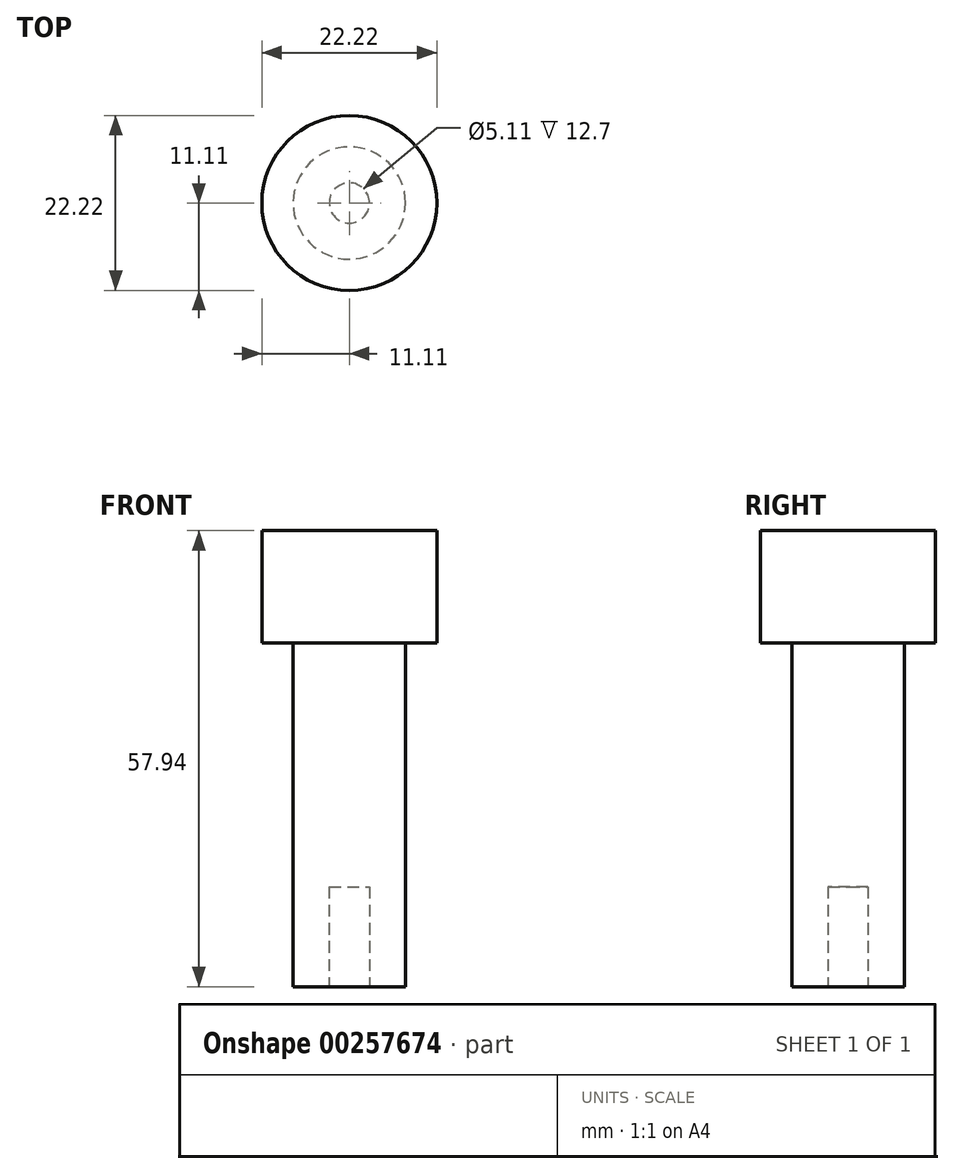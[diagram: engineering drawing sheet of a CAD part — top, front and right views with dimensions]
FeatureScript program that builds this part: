
annotation { "Feature Type Name" : "Feature", "Feature Type Description" : "" }
export const myFeature = defineFeature(function(context is Context, id is Id, definition is map)
    precondition{}
    {
        {
            var Q0;
            Q0=qCreatedBy(makeId("Top.planeOp"),FACE);
            var sketch = newSketch(context, id + "F0", { "sketchPlane" : qUnion([Q0])});
            skCircle(sketch, "E0", {"center": v(0, 0) * mm, "radius": 11.11 * mm});
            skSolve(sketch);
        }
        {
            var Q0;
            Q0=makeQuery(id+"F0.imprint","IMPRINT",FACE,{"disambiguationData":[TD([[makeQuery(id+"F0.imprint","IMPRINT",EDGE,{"derivedFrom":sQuery(id+"F0.wireOp",EDGE,"E0")}),1.0]])]});
            extrude(context, id + "F1", {"entities" : qUnion([Q0]), "endBound" : BoundingType.SYMMETRIC, "depth" : 14.27 * mm});
        }
        {
            var Q0;
            Q0=qCreatedBy(makeId("Top.planeOp"),FACE);
            var sketch = newSketch(context, id + "F2", { "sketchPlane" : qUnion([Q0])});
            skCircle(sketch, "E1", {"center": v(0, 0) * mm, "radius": 7.14 * mm});
            skSolve(sketch);
        }
        {
            var Q0;
            Q0 = qSketchRegion(id + "F2", true);
            var Q1;
            Q1=sQuery(id+"F2.wireOp",EDGE,"E1");
            extrude(context, id + "F3", {"entities" : qUnion([Q0]), "operationType" : NewBodyOperationType.ADD, "surfaceEntities" : qUnion([Q1]), "oppositeDirection" : true, "depth" : 50.8 * mm});
        }
        {
            var Q0;
            Q0=makeQuery(id+"F3.opExtrude","CAP_FACE",FACE,{"disambiguationData":[OSD([sQuery(id+"F2.wireOp",EDGE,"E1")])],"isStart":false});
            var sketch = newSketch(context, id + "F4", { "sketchPlane" : qUnion([Q0])});
            skCircle(sketch, "E2", {"center": v(0, 0) * mm, "radius": 2.55 * mm});
            skSolve(sketch);
        }
        {
            var Q0;
            Q0=makeQuery(id+"F4.imprint","IMPRINT",FACE,{"disambiguationData":[TD([[makeQuery(id+"F4.imprint","IMPRINT",EDGE,{"derivedFrom":sQuery(id+"F4.wireOp",EDGE,"E2")}),1.0]])]});
            extrude(context, id + "F5", {"entities" : qUnion([Q0]), "operationType" : NewBodyOperationType.REMOVE, "oppositeDirection" : true, "depth" : 12.7 * mm});
        }
    });
